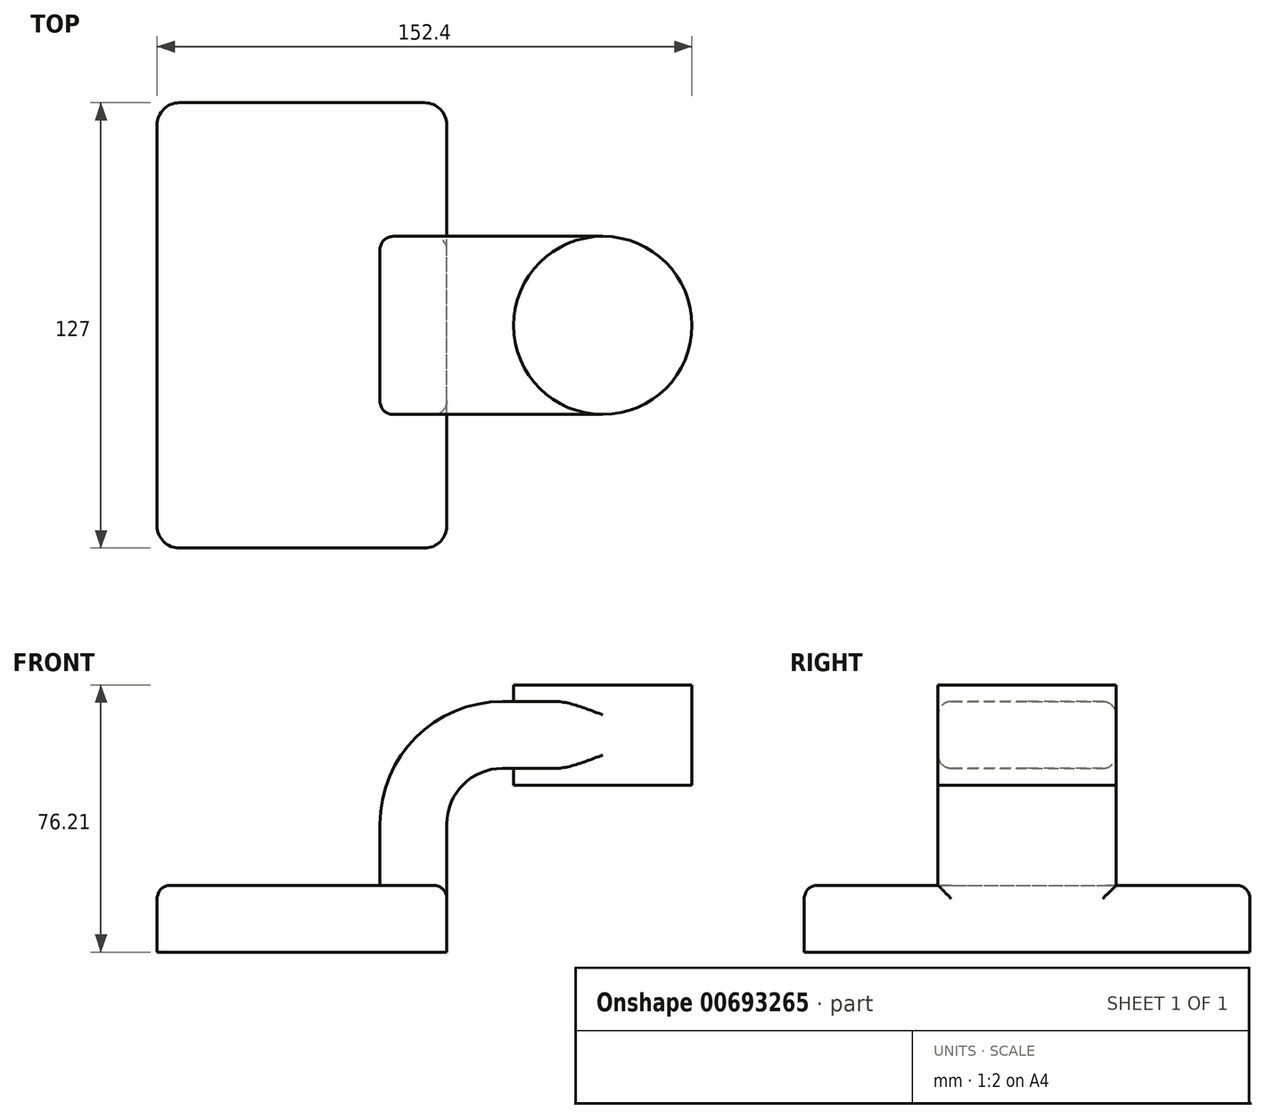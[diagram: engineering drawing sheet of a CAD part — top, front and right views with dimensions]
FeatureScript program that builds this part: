
annotation { "Feature Type Name" : "Feature", "Feature Type Description" : "" }
export const myFeature = defineFeature(function(context is Context, id is Id, definition is map)
    precondition{}
    {
        {
            var Q0;
            Q0=qCreatedBy(makeId("Front.planeOp"),FACE);
            var sketch = newSketch(context, id + "F0", { "sketchPlane" : qUnion([Q0])});
            skLineSegment(sketch, "E0.bottom", {"start": v(-41.27, -9.53) * mm, "end": v(41.28, -9.53) * mm});
            skLineSegment(sketch, "E0.top", {"start": v(-41.28, 9.52) * mm, "end": v(41.28, 9.52) * mm});
            skLineSegment(sketch, "E0.left", {"start": v(-41.28, -9.53) * mm, "end": v(-41.28, 9.53) * mm});
            skLineSegment(sketch, "E0.right", {"start": v(41.28, -9.53) * mm, "end": v(41.28, 9.52) * mm});
            skPoint(sketch, "E0.middle", {"position": v(0, 0) * mm});
            skLineSegment(sketch, "E1.bottom", {"start": v(60.32, 38.1) * mm, "end": v(111.12, 38.1) * mm});
            skLineSegment(sketch, "E1.top", {"start": v(60.32, 66.67) * mm, "end": v(111.12, 66.67) * mm});
            skLineSegment(sketch, "E1.left", {"start": v(60.32, 38.1) * mm, "end": v(60.32, 66.67) * mm});
            skLineSegment(sketch, "E1.right", {"start": v(111.12, 38.1) * mm, "end": v(111.12, 66.67) * mm});
            skPoint(sketch, "E1.middle", {"position": v(85.72, 52.39) * mm});
            skLineSegment(sketch, "E2", {"start": v(41.28, 9.52) * mm, "end": v(41.28, 27) * mm});
            skArc(sketch, "E3", {"start": v(41.27, 27) * mm, "mid": v(45.92, 38.23) * mm, "end": v(57.15, 42.88) * mm});
            skLineSegment(sketch, "E4", {"start": v(57.15, 42.88) * mm, "end": v(85.72, 42.88) * mm});
            skLineSegment(sketch, "E5.0", {"start": v(57.15, 61.93) * mm, "end": v(85.72, 61.93) * mm});
            skArc(sketch, "E5.1", {"start": v(22.22, 27) * mm, "mid": v(32.45, 51.7) * mm, "end": v(57.15, 61.93) * mm});
            skLineSegment(sketch, "E5.2", {"start": v(22.22, 9.52) * mm, "end": v(22.22, 27) * mm});
            skLineSegment(sketch, "E6", {"start": v(85.72, 38.1) * mm, "end": v(85.72, 66.67) * mm});
            skFitSpline(sketch, "E7", {"points": [v(-41.27, 9.52) * mm, v(57.15, 61.93) * mm], "startDerivative": vector(6.88, 72.02) * mm, "endDerivative": vector(111.9, -11.09) * mm});
            skSolve(sketch);
        }
        {
            var Q0;
            Q0=makeQuery(id+"F0.imprint","IMPRINT",FACE,{"disambiguationData":[TD([[makeQuery(id+"F0.imprint","IMPRINT",EDGE,{"derivedFrom":sQuery(id+"F0.wireOp",EDGE,"E0.bottom")}),1.0]])]});
            extrude(context, id + "F1", {"entities" : qUnion([Q0]), "endBound" : BoundingType.SYMMETRIC, "depth" : 127 * mm, "offsetDistance" : 25.4 * mm});
        }
        {
            var Q0;
            {var subQ1=sQuery(id+"F0.wireOp",EDGE,"E2");Q0=makeQuery(id+"F0.imprint","IMPRINT",FACE,{"disambiguationData":[TD([[makeQuery(id+"F0.imprint","IMPRINT",EDGE,{"derivedFrom":subQ1}),1.0]])]});}
            var Q1;
            {var subQ0=sQuery(id+"F0.wireOp",EDGE,"E4");var subQ1=sQuery(id+"F0.wireOp",EDGE,"E1.left");var subQ2=makeQuery(id+"F0.imprint","INTERSECT",VERTEX,{"derivedFrom":[subQ1,subQ0]});Q1=makeQuery(id+"F0.imprint","IMPRINT",FACE,{"disambiguationData":[TD([[makeQuery(id+"F0.imprint","IMPRINT",EDGE,{"disambiguationData":[TD([[subQ2,-1.0]])],"derivedFrom":subQ1}),-1.0]])]});}
            extrude(context, id + "F2", {"entities" : qUnion([Q0, Q1]), "operationType" : NewBodyOperationType.ADD, "endBound" : BoundingType.SYMMETRIC, "depth" : 50.8 * mm, "offsetDistance" : 25.4 * mm});
        }
        {
            var Q0;
            Q0=makeQuery(id+"F0.imprint","IMPRINT",FACE,{"disambiguationData":[TD([[makeQuery(id+"F0.imprint","IMPRINT",EDGE,{"derivedFrom":sQuery(id+"F0.wireOp",EDGE,"E5.1")}),1.0]])]});
            extrude(context, id + "F3", {"entities" : qUnion([Q0]), "operationType" : NewBodyOperationType.ADD, "endBound" : BoundingType.SYMMETRIC, "depth" : 15.88 * mm, "offsetDistance" : 25.4 * mm});
        }
        {
            var Q0;
            {var subQ0=sQuery(id+"F0.wireOp",EDGE,"E1.right");Q0=makeQuery(id+"F0.imprint","IMPRINT",FACE,{"disambiguationData":[TD([[makeQuery(id+"F0.imprint","IMPRINT",EDGE,{"derivedFrom":subQ0}),1.0]])]});}
            var Q1;
            Q1=sQuery(id+"F0.wireOp",EDGE,"E6");
            revolve(context, id + "F4", {"operationType" : NewBodyOperationType.ADD, "entities" : qUnion([Q0]), "axis" : qUnion([Q1]), "revolveType" : RevolveType.FULL});
        }
        {
            var Q0;
            Q0=makeQuery(id+"F1.opExtrude","CAP_EDGE",EDGE,{"disambiguationData":[OSD([sQuery(id+"F0.wireOp",EDGE,"E0.left")])],"isStart":false});
            var Q1;
            Q1=makeQuery(id+"F1.opExtrude","CAP_EDGE",EDGE,{"disambiguationData":[OSD([sQuery(id+"F0.wireOp",EDGE,"E0.right")])],"isStart":false});
            var Q2;
            Q2=makeQuery(id+"F1.opExtrude","CAP_EDGE",EDGE,{"disambiguationData":[OSD([sQuery(id+"F0.wireOp",EDGE,"E0.right")])],"isStart":true});
            var Q3;
            Q3=makeQuery(id+"F1.opExtrude","CAP_EDGE",EDGE,{"disambiguationData":[OSD([sQuery(id+"F0.wireOp",EDGE,"E0.left")])],"isStart":true});
            fillet(context, id + "F5", {"entities" : qUnion([Q0, Q1, Q2, Q3]), "radius" : 6.35 * mm, "tangentPropagation" : true, "allowEdgeOverflow" : false});
        }
        {
            var Q0;
            Q0=makeQuery(id+"F2.opExtrude","CAP_EDGE",EDGE,{"disambiguationData":[OSD([sQuery(id+"F0.wireOp",EDGE,"E5.1")])],"isStart":true});
            var Q1;
            Q1=makeQuery(id+"F2.opExtrude","CAP_EDGE",EDGE,{"disambiguationData":[OSD([sQuery(id+"F0.wireOp",EDGE,"E3")])],"isStart":true});
            var Q2;
            Q2=makeQuery(id+"F1.opExtrude","CAP_EDGE",EDGE,{"disambiguationData":[OSD([sQuery(id+"F0.wireOp",EDGE,"E0.top")])],"isStart":true});
            var Q3;
            Q3=makeQuery(id+"F2.opExtrude","CAP_EDGE",EDGE,{"disambiguationData":[OSD([sQuery(id+"F0.wireOp",EDGE,"E5.1")])],"isStart":false});
            var Q4;
            Q4=makeQuery(id+"F1.opExtrude","CAP_EDGE",EDGE,{"disambiguationData":[OSD([sQuery(id+"F0.wireOp",EDGE,"E0.top")])],"isStart":false});
            var Q5;
            Q5=makeQuery(id+"F2.opExtrude","CAP_EDGE",EDGE,{"disambiguationData":[OSD([sQuery(id+"F0.wireOp",EDGE,"E3")])],"isStart":false});
            fillet(context, id + "F6", {"entities" : qUnion([Q0, Q1, Q2, Q3, Q4, Q5]), "radius" : 3.8 * mm, "tangentPropagation" : true, "allowEdgeOverflow" : false});
        }
    });
